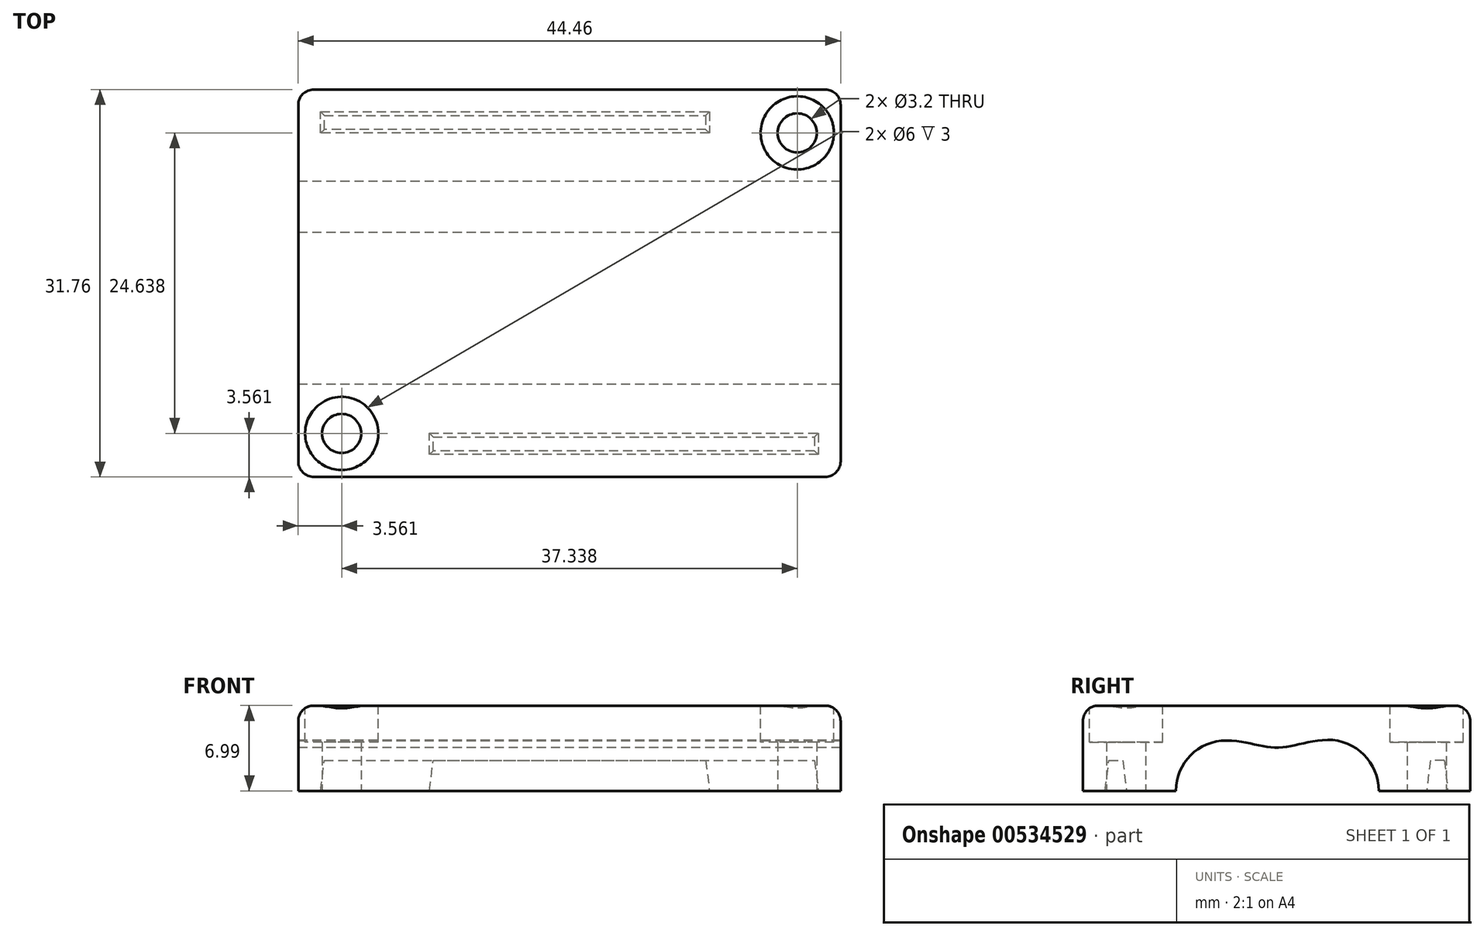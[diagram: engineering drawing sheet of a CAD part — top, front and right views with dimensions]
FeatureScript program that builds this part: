
annotation { "Feature Type Name" : "Feature", "Feature Type Description" : "" }
export const myFeature = defineFeature(function(context is Context, id is Id, definition is map)
    precondition{}
    {
        {
            var Q0;
            Q0=qCreatedBy(makeId("Top.planeOp"),FACE);
            var sketch = newSketch(context, id + "F0", { "sketchPlane" : qUnion([Q0])});
            skLineSegment(sketch, "E0.bottom", {"start": v(-38.1, 0) * mm, "end": v(38.1, 0) * mm});
            skLineSegment(sketch, "E0.top", {"start": v(-38.1, -4.13) * mm, "end": v(38.1, -4.13) * mm});
            skLineSegment(sketch, "E0.left", {"start": v(-38.1, 0) * mm, "end": v(-38.1, -4.13) * mm});
            skLineSegment(sketch, "E0.right", {"start": v(38.1, 0) * mm, "end": v(38.1, -4.13) * mm});
            skLineSegment(sketch, "E1.top", {"start": v(-38.1, 4.2) * mm, "end": v(38.1, 4.2) * mm});
            skLineSegment(sketch, "E1.left", {"start": v(-38.1, 0) * mm, "end": v(-38.1, 4.2) * mm});
            skLineSegment(sketch, "E1.right", {"start": v(38.1, 0) * mm, "end": v(38.1, 4.2) * mm});
            skLineSegment(sketch, "E2.MirrorCS", {"start": v(38.1, 8.38) * mm, "end": v(38.1, 4.2) * mm});
            skLineSegment(sketch, "E3.MirrorCS", {"start": v(-38.1, 8.38) * mm, "end": v(38.1, 8.38) * mm});
            skLineSegment(sketch, "E4.MirrorCS", {"start": v(-38.1, 8.38) * mm, "end": v(-38.1, 4.2) * mm});
            skLineSegment(sketch, "E5.MirrorCS", {"start": v(38.1, -8.25) * mm, "end": v(38.1, -4.12) * mm});
            skLineSegment(sketch, "E6.MirrorCS", {"start": v(-38.1, -8.25) * mm, "end": v(38.1, -8.25) * mm});
            skLineSegment(sketch, "E7.MirrorCS", {"start": v(-38.1, -8.25) * mm, "end": v(-38.1, -4.12) * mm});
            skSolve(sketch);
        }
        {
            var Q0;
            Q0=qCreatedBy(makeId("Top.planeOp"),FACE);
            var sketch = newSketch(context, id + "F1", { "sketchPlane" : qUnion([Q0])});
            skLineSegment(sketch, "E8.bottom", {"start": v(-22.23, 15.88) * mm, "end": v(22.23, 15.88) * mm});
            skLineSegment(sketch, "E8.top", {"start": v(-22.23, -15.88) * mm, "end": v(22.23, -15.88) * mm});
            skLineSegment(sketch, "E8.left", {"start": v(-22.23, 15.87) * mm, "end": v(-22.23, -15.88) * mm});
            skLineSegment(sketch, "E8.right", {"start": v(22.23, 15.88) * mm, "end": v(22.23, -15.87) * mm});
            skSolve(sketch);
        }
        {
            var Q0;
            Q0=qSketchRegion(id+"F1",true);
            extrude(context, id + "F2", {"entities" : qUnion([Q0]), "depth" : 7 * mm, "offsetDistance" : 25.4 * mm});
        }
        {
            var Q0;
            Q0=makeQuery(id+"F2.opExtrude","SWEPT_FACE",FACE,{"disambiguationData":[OSD([sQuery(id+"F1.wireOp",EDGE,"E8.right")])]});
            var sketch = newSketch(context, id + "F3", { "sketchPlane" : qUnion([Q0])});
            skLineSegment(sketch, "E9.0", {"start": v(-8.25, 0) * mm, "end": v(-4.12, 0) * mm});
            skLineSegment(sketch, "E10.0", {"start": v(8.38, 0) * mm, "end": v(4.2, 0) * mm});
            skArc(sketch, "E11", {"start": v(-4.13, 4.13) * mm, "mid": v(-8.25, 0) * mm, "end": v(-4.12, -4.13) * mm});
            skArc(sketch, "E12", {"start": v(4.2, -4.2) * mm, "mid": v(8.38, 0) * mm, "end": v(4.2, 4.2) * mm});
            skFitSpline(sketch, "E13", {"points": [v(-4.12, 4.13) * mm, v(0, 3.54) * mm, v(4.2, 4.2) * mm], "startDerivative": vector(10.24, -0.07) * mm, "endDerivative": vector(9.95, 0.46) * mm});
            skFitSpline(sketch, "E14", {"points": [v(-4.12, -4.13) * mm, v(0, -3.63) * mm, v(4.2, -4.2) * mm], "startDerivative": vector(7.18, -0.46) * mm, "endDerivative": vector(12.23, 0.06) * mm});
            skSolve(sketch);
        }
        {
            var Q0;
            Q0=qSketchRegion(id+"F3",true);
            var Q1;
            Q1=makeQuery(id+"F2.opExtrude","SWEPT_FACE",FACE,{"disambiguationData":[OSD([sQuery(id+"F1.wireOp",EDGE,"E8.left")])]});
            extrude(context, id + "F4", {"entities" : qUnion([Q0]), "operationType" : NewBodyOperationType.REMOVE, "endBound" : BoundingType.UP_TO_SURFACE, "oppositeDirection" : true, "depth" : 25.4 * mm, "endBoundEntityFace" : qUnion([Q1]), "offsetDistance" : 25.4 * mm});
        }
        {
            var Q0;
            Q0=qCreatedBy(makeId("Top.planeOp"),FACE);
            var sketch = newSketch(context, id + "F5", { "sketchPlane" : qUnion([Q0])});
            skCircle(sketch, "E15", {"center": v(-18.67, -12.32) * mm, "radius": 1.6 * mm});
            skCircle(sketch, "E16", {"center": v(18.67, 12.32) * mm, "radius": 1.6 * mm});
            skSolve(sketch);
        }
        {
            var Q0;
            Q0=qCreatedBy(makeId("Top.planeOp"),FACE);
            var sketch = newSketch(context, id + "F6", { "sketchPlane" : qUnion([Q0])});
            skLineSegment(sketch, "E17.bottom", {"start": v(11.47, 12.3) * mm, "end": v(-20.4, 12.3) * mm});
            skLineSegment(sketch, "E17.top", {"start": v(-20.4, 14.05) * mm, "end": v(11.47, 14.05) * mm});
            skLineSegment(sketch, "E17.left", {"start": v(11.47, 14.05) * mm, "end": v(11.47, 12.3) * mm});
            skLineSegment(sketch, "E17.right", {"start": v(-20.4, 14.05) * mm, "end": v(-20.4, 12.3) * mm});
            skLineSegment(sketch, "E18.bottom", {"start": v(-11.48, -12.3) * mm, "end": v(20.4, -12.3) * mm});
            skLineSegment(sketch, "E18.top", {"start": v(20.4, -14.05) * mm, "end": v(-11.48, -14.05) * mm});
            skLineSegment(sketch, "E18.left", {"start": v(-11.48, -12.3) * mm, "end": v(-11.48, -14.05) * mm});
            skLineSegment(sketch, "E18.right", {"start": v(20.4, -12.3) * mm, "end": v(20.4, -14.05) * mm});
            skSolve(sketch);
        }
        {
            var Q0;
            Q0 = qSketchRegion(id + "F6", true);
            extrude(context, id + "F7", {"entities" : qUnion([Q0]), "operationType" : NewBodyOperationType.REMOVE, "depth" : 2.5 * mm, "offsetDistance" : 25.4 * mm, "hasDraft" : true, "draftAngle" : 7 * degree, "draftPullDirection" : true});
        }
        {
            var Q0;
            Q0 = qSketchRegion(id + "F5", true);
            extrude(context, id + "F8", {"entities" : qUnion([Q0]), "operationType" : NewBodyOperationType.REMOVE, "depth" : 25.4 * mm, "offsetDistance" : 25.4 * mm});
        }
        {
            var Q0;
            Q0=makeQuery(id+"F2.opExtrude","CAP_FACE",FACE,{"disambiguationData":[OSD([sQuery(id+"F1.wireOp",EDGE,"E8.bottom"),sQuery(id+"F1.wireOp",EDGE,"E8.top"),sQuery(id+"F1.wireOp",EDGE,"E8.left"),sQuery(id+"F1.wireOp",EDGE,"E8.right")])],"isStart":false});
            var sketch = newSketch(context, id + "F9", { "sketchPlane" : qUnion([Q0])});
            skCircle(sketch, "E19.0", {"center": v(-18.67, -12.32) * mm, "radius": 1.6 * mm});
            skCircle(sketch, "E20.0", {"center": v(18.67, 12.32) * mm, "radius": 1.6 * mm});
            skCircle(sketch, "E21", {"center": v(-18.67, -12.32) * mm, "radius": 3 * mm});
            skCircle(sketch, "E22", {"center": v(18.67, 12.32) * mm, "radius": 3 * mm});
            skSolve(sketch);
        }
        {
            var Q0;
            Q0 = qSketchRegion(id + "F9", true);
            extrude(context, id + "F10", {"entities" : qUnion([Q0]), "operationType" : NewBodyOperationType.REMOVE, "oppositeDirection" : true, "depth" : 3 * mm, "offsetDistance" : 25.4 * mm});
        }
        {
            var Q0;
            Q0=makeQuery(id+"F2.opExtrude","CAP_EDGE",EDGE,{"disambiguationData":[OSD([sQuery(id+"F1.wireOp",EDGE,"E8.left")])],"isStart":false});
            var Q1;
            Q1=makeQuery(id+"F2.opExtrude","SWEPT_EDGE",EDGE,{"disambiguationData":[OSD([sQuery(id+"F1.wireOp",EDGE,"E8.top"),sQuery(id+"F1.wireOp",EDGE,"E8.left")])]});
            var Q2;
            Q2=makeQuery(id+"F2.opExtrude","CAP_EDGE",EDGE,{"disambiguationData":[OSD([sQuery(id+"F1.wireOp",EDGE,"E8.top")])],"isStart":false});
            var Q3;
            Q3=makeQuery(id+"F2.opExtrude","SWEPT_EDGE",EDGE,{"disambiguationData":[OSD([sQuery(id+"F1.wireOp",EDGE,"E8.top"),sQuery(id+"F1.wireOp",EDGE,"E8.right")])]});
            var Q4;
            Q4=makeQuery(id+"F2.opExtrude","CAP_EDGE",EDGE,{"disambiguationData":[OSD([sQuery(id+"F1.wireOp",EDGE,"E8.right")])],"isStart":false});
            var Q5;
            Q5=makeQuery(id+"F2.opExtrude","CAP_EDGE",EDGE,{"disambiguationData":[OSD([sQuery(id+"F1.wireOp",EDGE,"E8.bottom")])],"isStart":false});
            var Q6;
            Q6=makeQuery(id+"F2.opExtrude","SWEPT_EDGE",EDGE,{"disambiguationData":[OSD([sQuery(id+"F1.wireOp",EDGE,"E8.bottom"),sQuery(id+"F1.wireOp",EDGE,"E8.right")])]});
            var Q7;
            Q7=makeQuery(id+"F2.opExtrude","SWEPT_EDGE",EDGE,{"disambiguationData":[OSD([sQuery(id+"F1.wireOp",EDGE,"E8.bottom"),sQuery(id+"F1.wireOp",EDGE,"E8.left")])]});
            fillet(context, id + "F11", {"entities" : qUnion([Q0, Q1, Q2, Q3, Q4, Q5, Q6, Q7]), "radius" : 1.27 * mm, "tangentPropagation" : true, "allowEdgeOverflow" : false});
        }
    });
